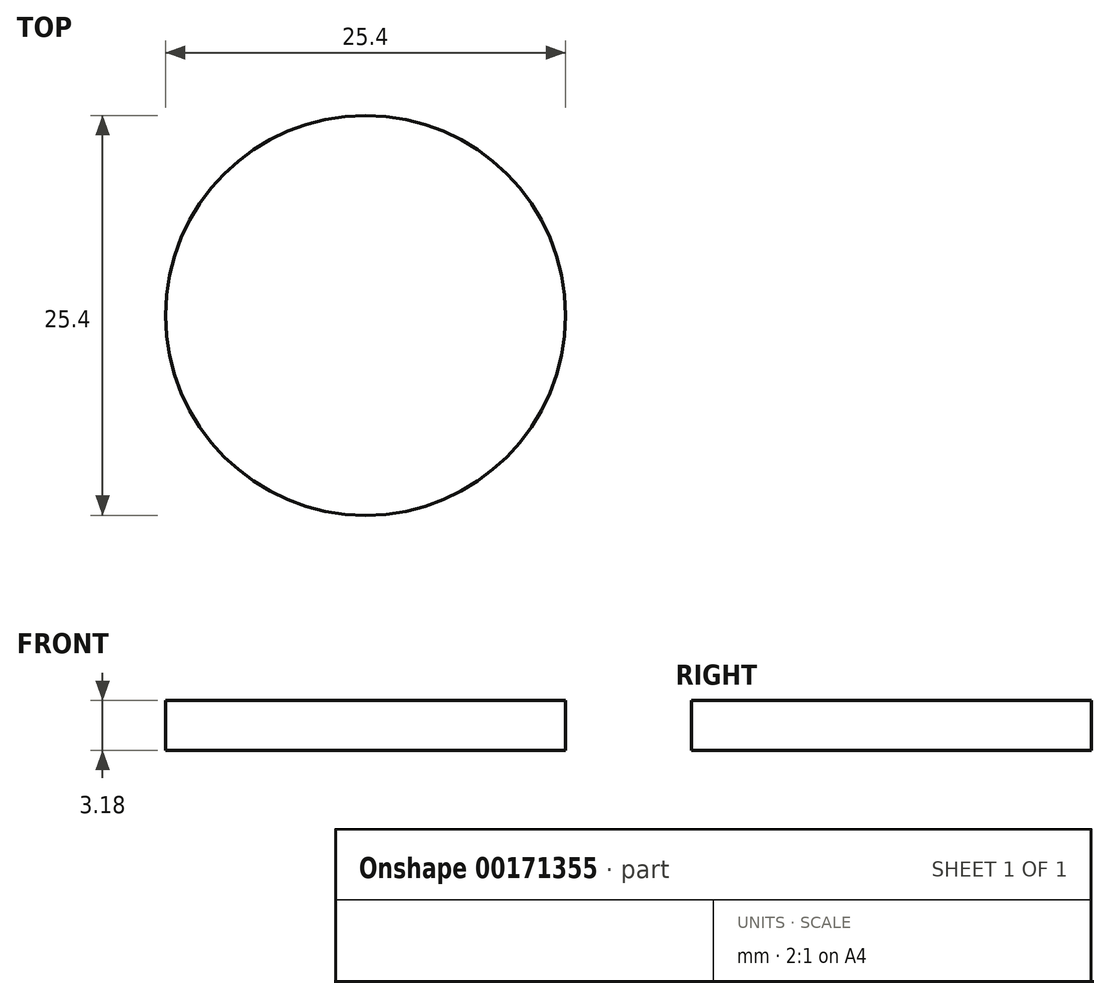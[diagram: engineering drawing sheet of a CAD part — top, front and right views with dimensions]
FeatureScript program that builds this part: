
annotation { "Feature Type Name" : "Feature", "Feature Type Description" : "" }
export const myFeature = defineFeature(function(context is Context, id is Id, definition is map)
    precondition{}
    {
        {
            var Q0;
            Q0=qCreatedBy(makeId("Top.planeOp"),FACE);
            var sketch = newSketch(context, id + "F0", { "sketchPlane" : qUnion([Q0])});
            skCircle(sketch, "E0", {"center": v(0, 0) * mm, "radius": 12.7 * mm});
            skSolve(sketch);
        }
        {
            var Q0;
            Q0 = qSketchRegion(id + "F0", true);
            extrude(context, id + "F1", {"entities" : qUnion([Q0]), "depth" : 3.17 * mm});
        }
    });
